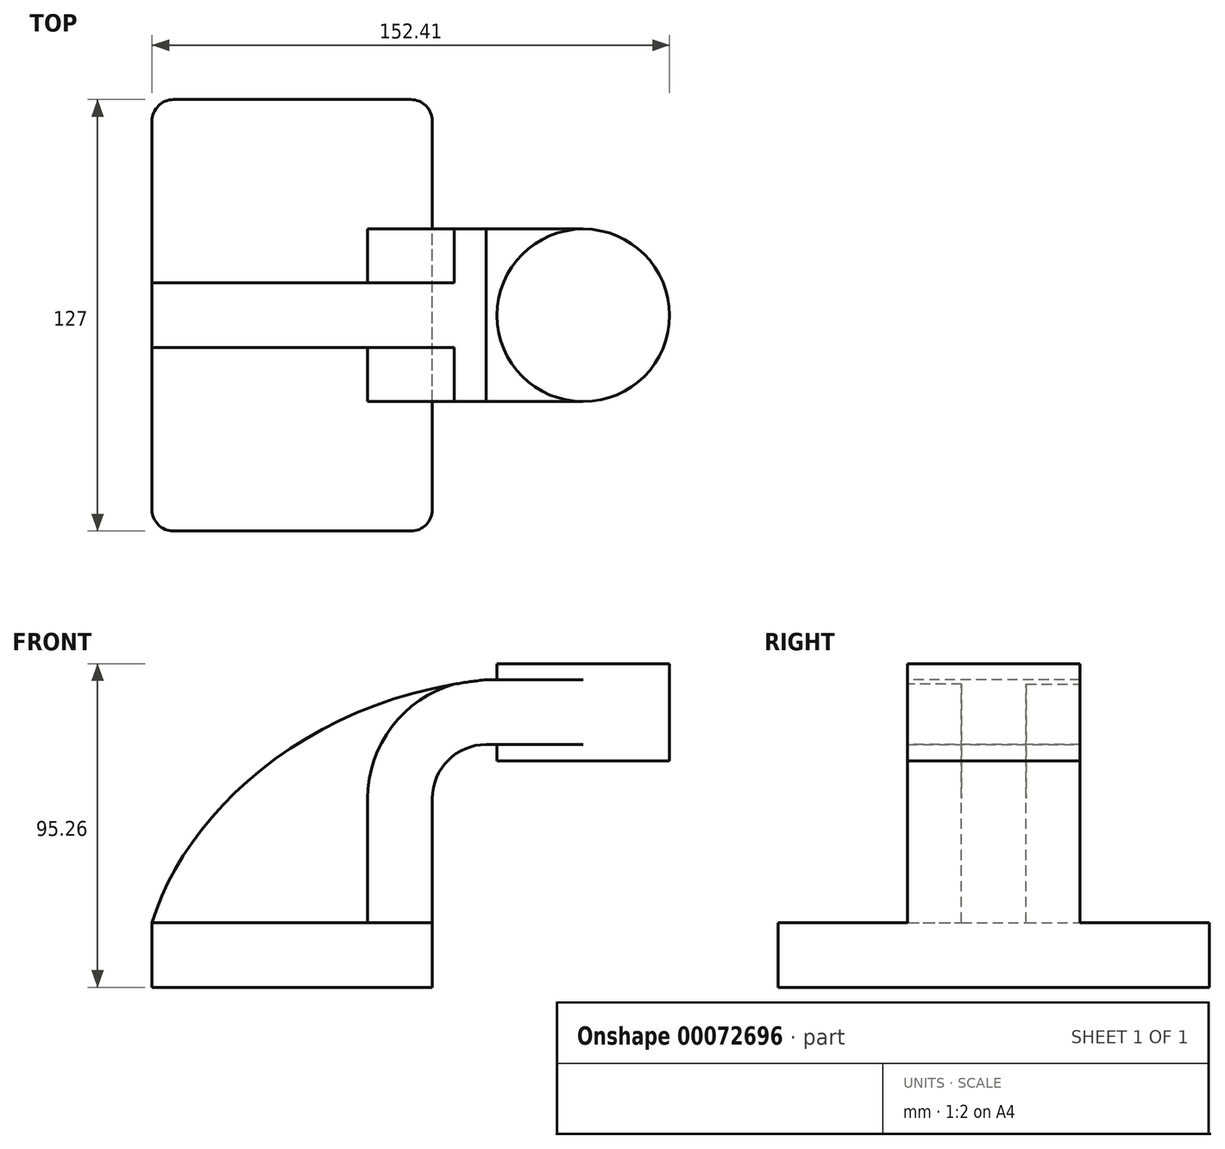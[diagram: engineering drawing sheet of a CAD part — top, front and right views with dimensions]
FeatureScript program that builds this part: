
annotation { "Feature Type Name" : "Feature", "Feature Type Description" : "" }
export const myFeature = defineFeature(function(context is Context, id is Id, definition is map)
    precondition{}
    {
        {
            var Q0;
            Q0=qCreatedBy(makeId("Front.planeOp"),FACE);
            var sketch = newSketch(context, id + "F0", { "sketchPlane" : qUnion([Q0])});
            skLineSegment(sketch, "E0.rect.bottom", {"start": v(-41.28, -9.53) * mm, "end": v(41.28, -9.53) * mm});
            skLineSegment(sketch, "E0.rect.top", {"start": v(-41.28, 9.53) * mm, "end": v(41.28, 9.53) * mm});
            skLineSegment(sketch, "E0.rect.left", {"start": v(-41.28, -9.53) * mm, "end": v(-41.28, 9.53) * mm});
            skLineSegment(sketch, "E0.rect.right", {"start": v(41.28, -9.53) * mm, "end": v(41.28, 9.53) * mm});
            skPoint(sketch, "E0.rect.middle", {"position": v(0, 0) * mm});
            skLineSegment(sketch, "E1.rect.bottom", {"start": v(111.12, 57.15) * mm, "end": v(60.32, 57.15) * mm});
            skLineSegment(sketch, "E1.rect.top", {"start": v(111.12, 85.73) * mm, "end": v(60.32, 85.73) * mm});
            skLineSegment(sketch, "E1.rect.left", {"start": v(111.12, 57.15) * mm, "end": v(111.12, 85.73) * mm});
            skLineSegment(sketch, "E1.rect.right", {"start": v(60.32, 57.15) * mm, "end": v(60.32, 85.73) * mm});
            skPoint(sketch, "E1.rect.middle", {"position": v(85.72, 71.44) * mm});
            skLineSegment(sketch, "E2", {"start": v(41.28, 9.53) * mm, "end": v(41.28, 46.05) * mm});
            skArc(sketch, "E3", {"start": v(41.27, 46.05) * mm, "mid": v(45.92, 57.28) * mm, "end": v(57.15, 61.93) * mm});
            skLineSegment(sketch, "E4", {"start": v(57.15, 61.93) * mm, "end": v(85.72, 61.93) * mm});
            skLineSegment(sketch, "E5.0", {"start": v(57.15, 80.98) * mm, "end": v(85.72, 80.98) * mm});
            skArc(sketch, "E5.1", {"start": v(22.23, 46.05) * mm, "mid": v(32.45, 70.75) * mm, "end": v(57.15, 80.98) * mm});
            skLineSegment(sketch, "E5.2", {"start": v(22.23, 9.53) * mm, "end": v(22.23, 46.05) * mm});
            skFitSpline(sketch, "E6", {"points": [v(-41.28, 9.52) * mm, v(57.15, 80.98) * mm], "startDerivative": vector(28.88, 96.14) * mm, "endDerivative": vector(157.76, 16.05) * mm});
            skLineSegment(sketch, "E7", {"start": v(85.72, 85.73) * mm, "end": v(85.72, 57.15) * mm});
            skSolve(sketch);
        }
        {
            var Q0;
            Q0=makeQuery(id+"F0.imprint","IMPRINT",FACE,{"disambiguationData":[TD([[makeQuery(id+"F0.imprint","IMPRINT",EDGE,{"derivedFrom":sQuery(id+"F0.wireOp",EDGE,"E0.rect.bottom")}),1.0]])]});
            extrude(context, id + "F1", {"entities" : qUnion([Q0]), "endBound" : BoundingType.SYMMETRIC, "depth" : 127 * mm});
        }
        {
            var Q0;
            {var subQ1=sQuery(id+"F0.wireOp",EDGE,"E2");Q0=makeQuery(id+"F0.imprint","IMPRINT",FACE,{"disambiguationData":[TD([[makeQuery(id+"F0.imprint","IMPRINT",EDGE,{"derivedFrom":subQ1}),1.0]])]});}
            var Q1;
            {var subQ0=sQuery(id+"F0.wireOp",EDGE,"E4");var subQ1=sQuery(id+"F0.wireOp",EDGE,"E1.rect.right");var subQ2=makeQuery(id+"F0.imprint","INTERSECT",VERTEX,{"derivedFrom":[subQ1,subQ0]});Q1=makeQuery(id+"F0.imprint","IMPRINT",FACE,{"disambiguationData":[TD([[makeQuery(id+"F0.imprint","IMPRINT",EDGE,{"disambiguationData":[TD([[subQ2,-1.0]])],"derivedFrom":subQ1}),-1.0]])]});}
            extrude(context, id + "F2", {"entities" : qUnion([Q0, Q1]), "operationType" : NewBodyOperationType.ADD, "endBound" : BoundingType.SYMMETRIC, "depth" : 50.8 * mm});
        }
        {
            var Q0;
            {var subQ3=sQuery(id+"F0.wireOp",EDGE,"E5.2");Q0=makeQuery(id+"F0.imprint","IMPRINT",FACE,{"disambiguationData":[TD([[makeQuery(id+"F0.imprint","IMPRINT",EDGE,{"derivedFrom":subQ3}),1.0]])]});}
            extrude(context, id + "F3", {"entities" : qUnion([Q0]), "operationType" : NewBodyOperationType.ADD, "endBound" : BoundingType.SYMMETRIC, "depth" : 19.05 * mm});
        }
        {
            var Q0;
            {var subQ4=sQuery(id+"F0.wireOp",EDGE,"E1.rect.left");Q0=makeQuery(id+"F0.imprint","IMPRINT",FACE,{"disambiguationData":[TD([[makeQuery(id+"F0.imprint","IMPRINT",EDGE,{"derivedFrom":subQ4}),1.0]])]});}
            var Q1;
            Q1=sQuery(id+"F0.wireOp",EDGE,"E7");
            revolve(context, id + "F4", {"operationType" : NewBodyOperationType.ADD, "entities" : qUnion([Q0]), "axis" : qUnion([Q1]), "revolveType" : RevolveType.FULL});
        }
        {
            var Q0;
            Q0=makeQuery(id+"F1.opExtrude","CAP_EDGE",EDGE,{"disambiguationData":[OSD([sQuery(id+"F0.wireOp",EDGE,"E0.rect.left")])],"isStart":false});
            var Q1;
            Q1=makeQuery(id+"F1.opExtrude","CAP_EDGE",EDGE,{"disambiguationData":[OSD([sQuery(id+"F0.wireOp",EDGE,"E0.rect.right")])],"isStart":false});
            var Q2;
            Q2=makeQuery(id+"F1.opExtrude","CAP_EDGE",EDGE,{"disambiguationData":[OSD([sQuery(id+"F0.wireOp",EDGE,"E0.rect.right")])],"isStart":true});
            var Q3;
            Q3=makeQuery(id+"F1.opExtrude","CAP_EDGE",EDGE,{"disambiguationData":[OSD([sQuery(id+"F0.wireOp",EDGE,"E0.rect.left")])],"isStart":true});
            fillet(context, id + "F5", {"entities" : qUnion([Q0, Q1, Q2, Q3]), "radius" : 6.35 * mm, "tangentPropagation" : true, "allowEdgeOverflow" : false});
        }
    });
